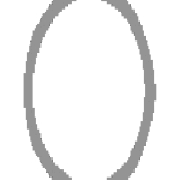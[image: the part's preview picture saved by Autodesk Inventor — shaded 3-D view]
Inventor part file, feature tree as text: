
AUTODESK INVENTOR PART (.ipt)
format: ipt  version: 2021 (Build 250183000, 183)  size: 109,056 bytes
history: native  units: in
note: dims shown in document units (in); Inventor stores cm internally (conversion verified against a paired STEP export)
features: other x4, sketch x3, plane x1
ambient origin geometry x8: Origin, YZ Plane, XZ Plane, XY Plane, X Axis, Y Axis, Z Axis, Center Point
bodies: Solid1 (feature_tree), Body (feature_tree)
feature tree (8):
  other  "Driven Length"
  other  "Frame Generator"
  other  "Start Plane"
  other  "End Plane"
  sketch  "Sketch"  dims[d2=31.4083in d4=-0.0in d5=31.4083in d6=0.12in d7=0.0in d8=90.0deg d9=31.4083in]
  sketch  "Sketch2"  dims[d0=1.0in]
  plane  "Work Plane3"
  sketch  "Sketch3"  dims[d1=0.065in]
